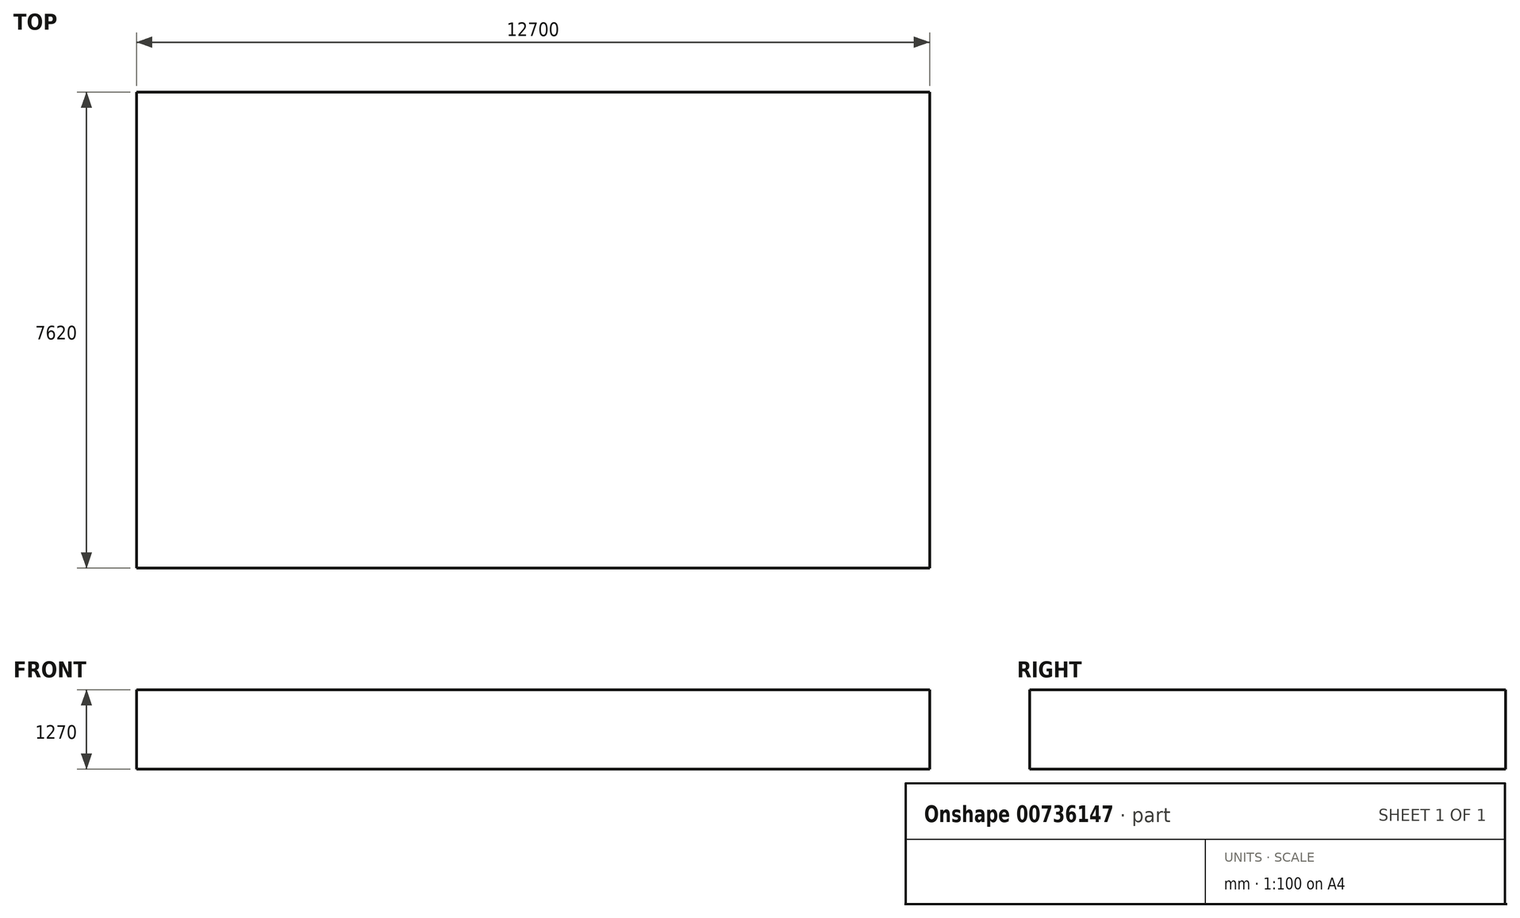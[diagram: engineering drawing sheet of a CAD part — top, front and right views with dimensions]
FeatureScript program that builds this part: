
annotation { "Feature Type Name" : "Feature", "Feature Type Description" : "" }
export const myFeature = defineFeature(function(context is Context, id is Id, definition is map)
    precondition{}
    {
        {
            var Q0;
            Q0=qCreatedBy(makeId("Top.planeOp"),FACE);
            var sketch = newSketch(context, id + "F0", { "sketchPlane" : qUnion([Q0])});
            skLineSegment(sketch, "E0.bottom", {"start": v(-9812.12, 3784.8) * mm, "end": v(2887.88, 3784.8) * mm});
            skLineSegment(sketch, "E0.top", {"start": v(-9812.12, -3835.2) * mm, "end": v(2887.88, -3835.2) * mm});
            skLineSegment(sketch, "E0.left", {"start": v(-9812.12, 3784.8) * mm, "end": v(-9812.12, -3835.2) * mm});
            skLineSegment(sketch, "E0.right", {"start": v(2887.88, 3784.8) * mm, "end": v(2887.88, -3835.2) * mm});
            skSolve(sketch);
        }
        {
            var Q0;
            Q0=makeQuery(id+"F0.imprint","IMPRINT",FACE,{"disambiguationData":[TD([[makeQuery(id+"F0.imprint","IMPRINT",EDGE,{"derivedFrom":sQuery(id+"F0.wireOp",EDGE,"E0.bottom")}),-1.0]])]});
            extrude(context, id + "F1", {"entities" : qUnion([Q0]), "depth" : 1270 * mm, "offsetDistance" : 25.4 * mm});
        }
    });
